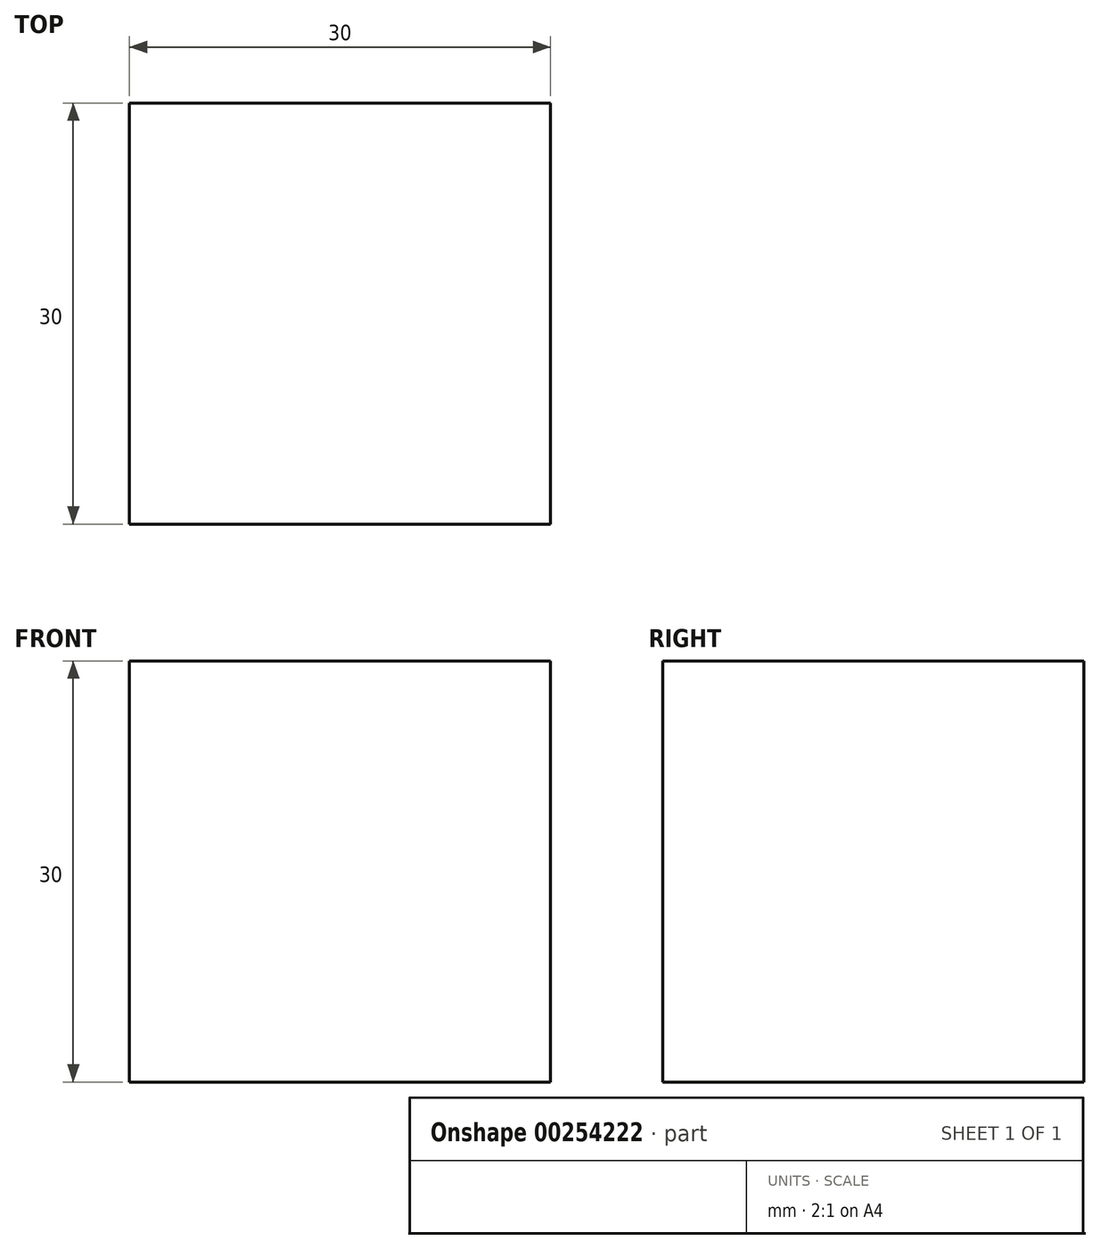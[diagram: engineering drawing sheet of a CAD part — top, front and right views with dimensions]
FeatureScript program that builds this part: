
annotation { "Feature Type Name" : "Feature", "Feature Type Description" : "" }
export const myFeature = defineFeature(function(context is Context, id is Id, definition is map)
    precondition{}
    {
        {
            var Q0;
            Q0=qCreatedBy(makeId("Front.planeOp"),FACE);
            var sketch = newSketch(context, id + "F0", { "sketchPlane" : qUnion([Q0])});
            skLineSegment(sketch, "E0.bottom", {"start": v(0, 0) * mm, "end": v(30, 0) * mm});
            skLineSegment(sketch, "E0.top", {"start": v(0, 30) * mm, "end": v(30, 30) * mm});
            skLineSegment(sketch, "E0.left", {"start": v(0, 0) * mm, "end": v(0, 30) * mm});
            skLineSegment(sketch, "E0.right", {"start": v(30, 0) * mm, "end": v(30, 30) * mm});
            skSolve(sketch);
        }
        {
            var Q0;
            Q0 = qSketchRegion(id + "F0", true);
            extrude(context, id + "F1", {"entities" : qUnion([Q0]), "depth" : 30 * mm});
        }
    });
